# Revit family: WSD_3D
name_source: partatom
category: Structural Connections
revit_build: Autodesk Revit 2014 (Build: 20140709_2115(x64)
units: mm (PartAtom-declared; Revit-internal decimal feet)

## types (1)
- WSD_3D
    A = 225 mm  [stored 0.738189 ft]
    B = 137 mm  [stored 0.449475 ft]
    C = 65 mm  [stored 0.213255 ft]
    Date Last Modified = August 28, 2018
    Default Elevation = 0 mm  [stored 0 ft]
    Description = Wind Secure™ tilslutningsbeslag
    Family Version = 1.0.0
    Manufacturer = Simpson Strong-Tie Company Inc.
    Model = WSD
    Model Disclaimer = Contact Simpson Strong-Tie Company Inc. for more information
    Product Material = Steel - Simpson - Galvanized
    Product Type = Wind Secure™ tilslutningsbeslag
    Provide Feedback = http://www.strongtie.com
    URL = www.strongtie.eu\s\WSD
    t = 3 mm  [stored 0.00984252 ft]

note: [stored X ft] marks values corroborated as IEEE doubles in the binary element streams (Revit-internal decimal feet)

## geometry (parser evidence)
native form markers: Blend x77, Sweep x1
no freeform markers — native parametric forms only
